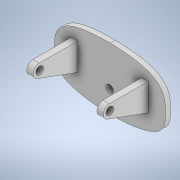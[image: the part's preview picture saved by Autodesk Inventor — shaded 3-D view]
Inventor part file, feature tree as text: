
AUTODESK INVENTOR PART (.ipt)
format: ipt  version: 2020.3 (Build 243373000, 373)  size: 164,352 bytes
history: native  units: in
note: dims shown in document units (in); Inventor stores cm internally (conversion verified against a paired STEP export)
features: extrude x3, sketch x3, direct_edit x1, projected_geometry x1, move_body x1
ambient origin geometry x8: Origin, YZ Plane, XZ Plane, XY Plane, X Axis, Y Axis, Z Axis, Center Point
bodies: Solid1 (feature_tree)
feature tree (9):
  extrude  "Extrusion1"  Depth=1.9685in TaperAngle=0.0deg
  extrude  "Extrusion2"  Depth=0.7874in
  extrude  "Extrusion3"  Depth=0.5343in TaperAngle=0.0deg
  direct_edit  "Direct Edit1"
  sketch  "Sketch1"  dims[d0=0.1575in d1=0.0in d9=1.9685in d10=0.0in]
  sketch  "Sketch2"  dims[d11=1.5748in d12=0.7874in]
  sketch  "Sketch3"  dims[d13=0.2362in d14=0.5343in d15=0.0in d16=0.0in d17=-0.3937in d18=0.0in]
  projected_geometry  "Projected Loop1"
  move_body  "Move1"
